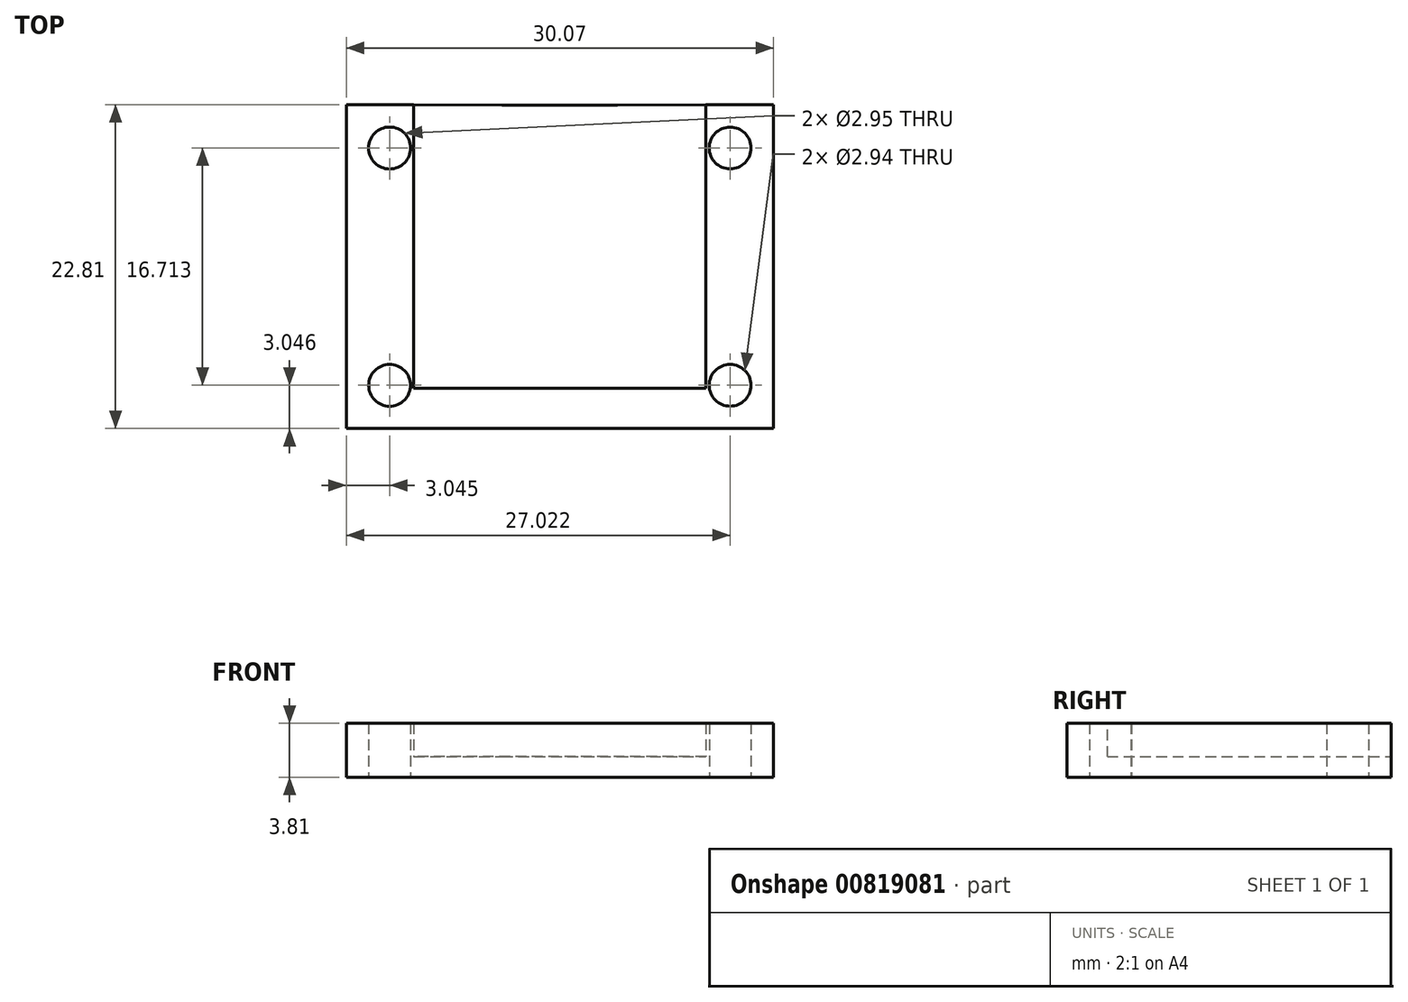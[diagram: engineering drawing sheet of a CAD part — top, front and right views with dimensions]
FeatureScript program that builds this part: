
annotation { "Feature Type Name" : "Feature", "Feature Type Description" : "" }
export const myFeature = defineFeature(function(context is Context, id is Id, definition is map)
    precondition{}
    {
        {
            var Q0;
            Q0=qCreatedBy(makeId("Top.planeOp"),FACE);
            var sketch = newSketch(context, id + "F0", { "sketchPlane" : qUnion([Q0])});
            skLineSegment(sketch, "E0.bottom", {"start": v(10.31, -9.2) * mm, "end": v(-10.31, -9.2) * mm});
            skLineSegment(sketch, "E0.left", {"start": v(10.31, -9.2) * mm, "end": v(10.31, 9.2) * mm});
            skLineSegment(sketch, "E0.right", {"start": v(-10.31, -9.2) * mm, "end": v(-10.31, 9.2) * mm});
            skPoint(sketch, "E0.middle", {"position": v(0, 0) * mm});
            skLineSegment(sketch, "E1.bottom", {"start": v(4.06, 3.08) * mm, "end": v(-4.06, 3.08) * mm});
            skLineSegment(sketch, "E1.left", {"start": v(4.06, 3.08) * mm, "end": v(4.06, 9.18) * mm});
            skLineSegment(sketch, "E1.right", {"start": v(-4.06, 3.08) * mm, "end": v(-4.06, 9.18) * mm});
            skPoint(sketch, "E1.middle", {"position": v(0, 6.13) * mm});
            skLineSegment(sketch, "E2", {"start": v(-10.31, 9.2) * mm, "end": v(-4.06, 9.18) * mm});
            skLineSegment(sketch, "E3", {"start": v(4.06, 9.18) * mm, "end": v(10.31, 9.2) * mm});
            skSolve(sketch);
        }
        {
            var Q0;
            Q0=makeQuery(id+"F0.imprint","IMPRINT",FACE,{"disambiguationData":[TD([[makeQuery(id+"F0.imprint","IMPRINT",EDGE,{"derivedFrom":sQuery(id+"F0.wireOp",EDGE,"E0.bottom")}),-1.0]])]});
            extrude(context, id + "F1", {"entities" : qUnion([Q0]), "depth" : 3.8 * mm, "offsetDistance" : 25.4 * mm});
        }
        {
            var Q0;
            Q0=makeQuery(id+"F1.opExtrude","SWEPT_FACE",FACE,{"disambiguationData":[OSD([sQuery(id+"F0.wireOp",EDGE,"E1.bottom")])]});
            var sketch = newSketch(context, id + "F2", { "sketchPlane" : qUnion([Q0])});
            skLineSegment(sketch, "E4.bottom", {"start": v(4.06, 3.81) * mm, "end": v(-4.06, 3.81) * mm});
            skLineSegment(sketch, "E4.top", {"start": v(4.06, 1.9) * mm, "end": v(-4.06, 1.9) * mm});
            skLineSegment(sketch, "E4.left", {"start": v(4.06, 3.81) * mm, "end": v(4.06, 1.9) * mm});
            skLineSegment(sketch, "E4.right", {"start": v(-4.06, 3.81) * mm, "end": v(-4.06, 1.9) * mm});
            skSolve(sketch);
        }
        {
            var Q0;
            Q0=makeQuery(id+"F2.imprint","IMPRINT",FACE,{"disambiguationData":[TD([[makeQuery(id+"F2.imprint","IMPRINT",EDGE,{"derivedFrom":sQuery(id+"F2.wireOp",EDGE,"E4.bottom")}),-1.0]])]});
            var Q1;
            Q1=makeQuery(id+"F1.opExtrude","SWEPT_FACE",FACE,{"disambiguationData":[OSD([sQuery(id+"F0.wireOp",EDGE,"E0.bottom")])]});
            extrude(context, id + "F3", {"entities" : qUnion([Q0, Q1]), "operationType" : NewBodyOperationType.ADD, "oppositeDirection" : true, "depth" : 1.85 * mm, "offsetDistance" : 25.4 * mm});
        }
        {
            var Q0;
            {var subQ0=sQuery(id+"F0.wireOp",EDGE,"E0.right");Q0=makeQuery(id+"F3.boolean.opBoolean","MERGE",FACE,{"derivedFrom":[makeQuery(id+"F1.opExtrude","SWEPT_FACE",FACE,{"disambiguationData":[OSD([subQ0])]}),makeQuery(id+"F3.opExtrude","SWEPT_FACE",FACE,{"disambiguationData":[OSD([sQuery(id+"F0.wireOp",EDGE,"E0.bottom"),subQ0])]})]});}
            extrude(context, id + "F4", {"entities" : qUnion([Q0]), "operationType" : NewBodyOperationType.ADD, "depth" : 2.18 * mm, "offsetDistance" : 25.4 * mm});
        }
        {
            var Q0;
            {var subQ0=sQuery(id+"F0.wireOp",EDGE,"E0.left");Q0=makeQuery(id+"F3.boolean.opBoolean","MERGE",FACE,{"derivedFrom":[makeQuery(id+"F1.opExtrude","SWEPT_FACE",FACE,{"disambiguationData":[OSD([subQ0])]}),makeQuery(id+"F3.opExtrude","SWEPT_FACE",FACE,{"disambiguationData":[OSD([sQuery(id+"F0.wireOp",EDGE,"E0.bottom"),subQ0])]})]});}
            extrude(context, id + "F5", {"entities" : qUnion([Q0]), "operationType" : NewBodyOperationType.ADD, "depth" : 2.18 * mm, "offsetDistance" : 25.4 * mm});
        }
        {
            var Q0;
            Q0=makeQuery(id+"F1.opExtrude","SWEPT_FACE",FACE,{"disambiguationData":[OSD([sQuery(id+"F0.wireOp",EDGE,"E1.bottom")])]});
            var sketch = newSketch(context, id + "F6", { "sketchPlane" : qUnion([Q0])});
            skLineSegment(sketch, "E5.bottom", {"start": v(-4.06, 3.81) * mm, "end": v(4.06, 3.81) * mm});
            skLineSegment(sketch, "E5.top", {"start": v(-4.06, 1.68) * mm, "end": v(4.06, 1.68) * mm});
            skLineSegment(sketch, "E5.left", {"start": v(-4.06, 3.81) * mm, "end": v(-4.06, 1.68) * mm});
            skLineSegment(sketch, "E5.right", {"start": v(4.06, 3.81) * mm, "end": v(4.06, 1.68) * mm});
            skSolve(sketch);
        }
        {
            var Q0;
            Q0=makeQuery(id+"F6.imprint","IMPRINT",FACE,{"disambiguationData":[TD([[makeQuery(id+"F6.imprint","IMPRINT",EDGE,{"derivedFrom":sQuery(id+"F6.wireOp",EDGE,"E5.bottom")}),-1.0]])]});
            extrude(context, id + "F7", {"entities" : qUnion([Q0]), "operationType" : NewBodyOperationType.ADD, "depth" : 6.1 * mm, "offsetDistance" : 25.4 * mm});
        }
        {
            var Q0;
            {var subQ0=sQuery(id+"F0.wireOp",EDGE,"E0.left");var subQ1=sQuery(id+"F0.wireOp",EDGE,"E0.bottom");var subQ2=sQuery(id+"F0.wireOp",EDGE,"E0.right");Q0=makeQuery(id+"F5.boolean.opBoolean","MERGE",FACE,{"derivedFrom":[makeQuery(id+"F4.boolean.opBoolean","MERGE",FACE,{"derivedFrom":[makeQuery(id+"F3.boolean.opBoolean","MERGE",FACE,{"derivedFrom":[makeQuery(id+"F1.opExtrude","CAP_FACE",FACE,{"disambiguationData":[OSD([subQ1,subQ0,subQ2,sQuery(id+"F0.wireOp",EDGE,"E1.bottom"),sQuery(id+"F0.wireOp",EDGE,"E1.left"),sQuery(id+"F0.wireOp",EDGE,"E1.right"),sQuery(id+"F0.wireOp",EDGE,"E2"),sQuery(id+"F0.wireOp",EDGE,"E3")])],"isStart":true}),makeQuery(id+"F3.opExtrude","SWEPT_FACE",FACE,{"disambiguationData":[OSD([subQ1]),TDD([makeQuery(id+"F1.opExtrude","CAP_EDGE",EDGE,{"disambiguationData":[OSD([subQ1])],"isStart":true})])]})]}),makeQuery(id+"F4.opExtrude","SWEPT_FACE",FACE,{"disambiguationData":[OSD([subQ1,subQ2]),TDD([makeQuery(id+"F3.boolean.opBoolean","MERGE",EDGE,{"derivedFrom":[makeQuery(id+"F1.opExtrude","CAP_EDGE",EDGE,{"disambiguationData":[OSD([subQ2])],"isStart":true}),makeQuery(id+"F3.opExtrude","SWEPT_EDGE",EDGE,{"disambiguationData":[OSD([subQ1,subQ2]),TDD([makeQuery(id+"F1.opExtrude","CAP_VERTEX",VERTEX,{"disambiguationData":[OSD([subQ1,subQ2])],"isStart":true})])]})]})])]})]}),makeQuery(id+"F5.opExtrude","SWEPT_FACE",FACE,{"disambiguationData":[OSD([subQ1,subQ0]),TDD([makeQuery(id+"F3.boolean.opBoolean","MERGE",EDGE,{"derivedFrom":[makeQuery(id+"F1.opExtrude","CAP_EDGE",EDGE,{"disambiguationData":[OSD([subQ0])],"isStart":true}),makeQuery(id+"F3.opExtrude","SWEPT_EDGE",EDGE,{"disambiguationData":[OSD([subQ1,subQ0]),TDD([makeQuery(id+"F1.opExtrude","CAP_VERTEX",VERTEX,{"disambiguationData":[OSD([subQ1,subQ0])],"isStart":true})])]})]})])]})]});}
            var sketch = newSketch(context, id + "F8", { "sketchPlane" : qUnion([Q0])});
            skLineSegment(sketch, "E6.bottom", {"start": v(-9.07, 8.52) * mm, "end": v(9.07, 8.52) * mm});
            skLineSegment(sketch, "E6.top", {"start": v(-9.07, 0) * mm, "end": v(9.07, 0) * mm});
            skLineSegment(sketch, "E6.left", {"start": v(-9.07, 8.52) * mm, "end": v(-9.07, 0) * mm});
            skLineSegment(sketch, "E6.right", {"start": v(9.07, 8.52) * mm, "end": v(9.07, 0) * mm});
            skSolve(sketch);
        }
        {
            var Q0;
            Q0=makeQuery(id+"F8.imprint","IMPRINT",FACE,{"disambiguationData":[TD([[makeQuery(id+"F8.imprint","IMPRINT",EDGE,{"derivedFrom":sQuery(id+"F8.wireOp",EDGE,"E6.bottom")}),-1.0]])]});
            extrude(context, id + "F9", {"entities" : qUnion([Q0]), "operationType" : NewBodyOperationType.REMOVE, "oppositeDirection" : true, "depth" : 1.55 * mm, "offsetDistance" : 25.4 * mm});
        }
        {
            var Q0;
            {var subQ0=sQuery(id+"F0.wireOp",EDGE,"E0.left");var subQ1=sQuery(id+"F0.wireOp",EDGE,"E0.bottom");var subQ2=sQuery(id+"F0.wireOp",EDGE,"E0.right");Q0=makeQuery(id+"F7.boolean.opBoolean","MERGE",FACE,{"derivedFrom":[makeQuery(id+"F5.boolean.opBoolean","MERGE",FACE,{"derivedFrom":[makeQuery(id+"F4.boolean.opBoolean","MERGE",FACE,{"derivedFrom":[makeQuery(id+"F3.boolean.opBoolean","MERGE",FACE,{"derivedFrom":[makeQuery(id+"F1.opExtrude","CAP_FACE",FACE,{"disambiguationData":[OSD([subQ1,subQ0,subQ2,sQuery(id+"F0.wireOp",EDGE,"E1.bottom"),sQuery(id+"F0.wireOp",EDGE,"E1.left"),sQuery(id+"F0.wireOp",EDGE,"E1.right"),sQuery(id+"F0.wireOp",EDGE,"E2"),sQuery(id+"F0.wireOp",EDGE,"E3")])],"isStart":false}),makeQuery(id+"F3.opExtrude","SWEPT_FACE",FACE,{"disambiguationData":[OSD([subQ1]),TDD([makeQuery(id+"F1.opExtrude","CAP_EDGE",EDGE,{"disambiguationData":[OSD([subQ1])],"isStart":false})])]})]}),makeQuery(id+"F4.opExtrude","SWEPT_FACE",FACE,{"disambiguationData":[OSD([subQ1,subQ2]),TDD([makeQuery(id+"F3.boolean.opBoolean","MERGE",EDGE,{"derivedFrom":[makeQuery(id+"F1.opExtrude","CAP_EDGE",EDGE,{"disambiguationData":[OSD([subQ2])],"isStart":false}),makeQuery(id+"F3.opExtrude","SWEPT_EDGE",EDGE,{"disambiguationData":[OSD([subQ1,subQ2]),TDD([makeQuery(id+"F1.opExtrude","CAP_VERTEX",VERTEX,{"disambiguationData":[OSD([subQ1,subQ2])],"isStart":false})])]})]})])]})]}),makeQuery(id+"F5.opExtrude","SWEPT_FACE",FACE,{"disambiguationData":[OSD([subQ1,subQ0]),TDD([makeQuery(id+"F3.boolean.opBoolean","MERGE",EDGE,{"derivedFrom":[makeQuery(id+"F1.opExtrude","CAP_EDGE",EDGE,{"disambiguationData":[OSD([subQ0])],"isStart":false}),makeQuery(id+"F3.opExtrude","SWEPT_EDGE",EDGE,{"disambiguationData":[OSD([subQ1,subQ0]),TDD([makeQuery(id+"F1.opExtrude","CAP_VERTEX",VERTEX,{"disambiguationData":[OSD([subQ1,subQ0])],"isStart":false})])]})]})])]})]}),makeQuery(id+"F7.opExtrude","SWEPT_FACE",FACE,{"disambiguationData":[OSD([sQuery(id+"F6.wireOp",EDGE,"E5.bottom")])]})]});}
            var sketch = newSketch(context, id + "F10", { "sketchPlane" : qUnion([Q0])});
            skLineSegment(sketch, "E7.bottom", {"start": v(-12.5, 9.2) * mm, "end": v(12.5, 9.2) * mm});
            skLineSegment(sketch, "E7.top", {"start": v(-12.5, -11.06) * mm, "end": v(12.5, -11.06) * mm});
            skLineSegment(sketch, "E7.left", {"start": v(-12.5, 9.2) * mm, "end": v(-12.5, -11.06) * mm});
            skLineSegment(sketch, "E7.right", {"start": v(12.5, 9.2) * mm, "end": v(12.5, -11.06) * mm});
            skSolve(sketch);
        }
        {
            var Q0;
            Q0=makeQuery(id+"F4.opExtrude","CAP_FACE",FACE,{"disambiguationData":[OSD([sQuery(id+"F0.wireOp",EDGE,"E0.bottom"),sQuery(id+"F0.wireOp",EDGE,"E0.right")])],"isStart":false});
            extrude(context, id + "F11", {"entities" : qUnion([Q0]), "operationType" : NewBodyOperationType.ADD, "depth" : 2.54 * mm, "offsetDistance" : 25.4 * mm});
        }
        {
            var Q0;
            Q0=makeQuery(id+"F5.opExtrude","CAP_FACE",FACE,{"disambiguationData":[OSD([sQuery(id+"F0.wireOp",EDGE,"E0.bottom"),sQuery(id+"F0.wireOp",EDGE,"E0.left")])],"isStart":false});
            extrude(context, id + "F12", {"entities" : qUnion([Q0]), "operationType" : NewBodyOperationType.ADD, "depth" : 2.54 * mm, "offsetDistance" : 25.4 * mm});
        }
        {
            var Q0;
            {var subQ0=sQuery(id+"F0.wireOp",EDGE,"E0.left");var subQ1=sQuery(id+"F0.wireOp",EDGE,"E0.bottom");var subQ2=makeQuery(id+"F3.opExtrude","CAP_EDGE",EDGE,{"disambiguationData":[OSD([subQ1,subQ0])],"isStart":false});var subQ3=sQuery(id+"F0.wireOp",EDGE,"E0.right");var subQ4=makeQuery(id+"F3.opExtrude","CAP_EDGE",EDGE,{"disambiguationData":[OSD([subQ1,subQ3])],"isStart":false});Q0=makeQuery(id+"F12.boolean.opBoolean","MERGE",FACE,{"derivedFrom":[makeQuery(id+"F11.boolean.opBoolean","MERGE",FACE,{"derivedFrom":[makeQuery(id+"F5.boolean.opBoolean","MERGE",FACE,{"derivedFrom":[makeQuery(id+"F4.boolean.opBoolean","MERGE",FACE,{"derivedFrom":[makeQuery(id+"F3.opExtrude","CAP_FACE",FACE,{"disambiguationData":[OSD([subQ1])],"isStart":false}),makeQuery(id+"F4.opExtrude","SWEPT_FACE",FACE,{"disambiguationData":[OSD([subQ1,subQ3]),TDD([subQ4])]})]}),makeQuery(id+"F5.opExtrude","SWEPT_FACE",FACE,{"disambiguationData":[OSD([subQ1,subQ0]),TDD([subQ2])]})]}),makeQuery(id+"F11.opExtrude","SWEPT_FACE",FACE,{"disambiguationData":[OSD([subQ1,subQ3]),TDD([makeQuery(id+"F4.opExtrude","CAP_EDGE",EDGE,{"disambiguationData":[OSD([subQ1,subQ3]),TDD([subQ4])],"isStart":false})])]})]}),makeQuery(id+"F12.opExtrude","SWEPT_FACE",FACE,{"disambiguationData":[OSD([subQ1,subQ0]),TDD([makeQuery(id+"F5.opExtrude","CAP_EDGE",EDGE,{"disambiguationData":[OSD([subQ1,subQ0]),TDD([subQ2])],"isStart":false})])]})]});}
            extrude(context, id + "F13", {"entities" : qUnion([Q0]), "operationType" : NewBodyOperationType.ADD, "depth" : 2.54 * mm, "offsetDistance" : 25.4 * mm});
        }
        {
            var Q0;
            Q0=makeQuery(id+"F9.boolean.opBoolean","COPY",FACE,{"derivedFrom":makeQuery(id+"F9.opExtrude","CAP_FACE",FACE,{"disambiguationData":[OSD([sQuery(id+"F8.wireOp",EDGE,"E6.bottom"),sQuery(id+"F8.wireOp",EDGE,"E6.top"),sQuery(id+"F8.wireOp",EDGE,"E6.left"),sQuery(id+"F8.wireOp",EDGE,"E6.right")])],"isStart":false})});
            extrude(context, id + "F14", {"entities" : qUnion([Q0]), "operationType" : NewBodyOperationType.REMOVE, "oppositeDirection" : true, "depth" : 0.81 * mm, "offsetDistance" : 25.4 * mm});
        }
        {
            var Q0;
            Q0=makeQuery(id+"F1.opExtrude","SWEPT_BODY",BODY,{"disambiguationData":[OSD([sQuery(id+"F0.wireOp",EDGE,"E0.bottom"),sQuery(id+"F0.wireOp",EDGE,"E0.left"),sQuery(id+"F0.wireOp",EDGE,"E0.right"),sQuery(id+"F0.wireOp",EDGE,"E1.bottom"),sQuery(id+"F0.wireOp",EDGE,"E1.left"),sQuery(id+"F0.wireOp",EDGE,"E1.right"),sQuery(id+"F0.wireOp",EDGE,"E2"),sQuery(id+"F0.wireOp",EDGE,"E3")])]});
            var Q1;
            Q1=sQuery(id+"F10.wireOp",EDGE,"E7.right");
            transform(context, id + "F15", {"entities" : qUnion([Q0]), "transformType" : TransformType.ROTATION, "transformAxis" : qUnion([Q1]), "angle" : 180 * degree, "oppositeDirection" : true, "makeCopy" : false});
        }
        {
            var Q0;
            {var subQ0=sQuery(id+"F8.wireOp",EDGE,"E6.bottom");Q0=makeQuery(id+"F14.boolean.opBoolean","MERGE",FACE,{"derivedFrom":[makeQuery(id+"F9.boolean.opBoolean","COPY",FACE,{"derivedFrom":makeQuery(id+"F9.opExtrude","SWEPT_FACE",FACE,{"disambiguationData":[OSD([subQ0])]})}),makeQuery(id+"F14.opExtrude","SWEPT_FACE",FACE,{"disambiguationData":[OSD([subQ0])]})]});}
            extrude(context, id + "F16", {"entities" : qUnion([Q0]), "operationType" : NewBodyOperationType.REMOVE, "oppositeDirection" : true, "depth" : 2.24 * mm, "offsetDistance" : 25.4 * mm});
        }
        {
            var Q0;
            {var subQ0=sQuery(id+"F0.wireOp",EDGE,"E0.left");var subQ1=sQuery(id+"F0.wireOp",EDGE,"E0.bottom");var subQ2=makeQuery(id+"F1.opExtrude","CAP_VERTEX",VERTEX,{"disambiguationData":[OSD([subQ1,subQ0])],"isStart":false});var subQ3=makeQuery(id+"F3.opExtrude","CAP_VERTEX",VERTEX,{"disambiguationData":[OSD([subQ1,subQ0]),TDD([subQ2])],"isStart":false});var subQ4=sQuery(id+"F0.wireOp",EDGE,"E0.right");var subQ5=makeQuery(id+"F1.opExtrude","CAP_VERTEX",VERTEX,{"disambiguationData":[OSD([subQ1,subQ4])],"isStart":false});var subQ6=makeQuery(id+"F3.opExtrude","CAP_VERTEX",VERTEX,{"disambiguationData":[OSD([subQ1,subQ4]),TDD([subQ5])],"isStart":false});var subQ7=makeQuery(id+"F1.opExtrude","CAP_EDGE",EDGE,{"disambiguationData":[OSD([subQ1])],"isStart":false});var subQ8=makeQuery(id+"F3.boolean.opBoolean","MERGE",EDGE,{"derivedFrom":[makeQuery(id+"F1.opExtrude","CAP_EDGE",EDGE,{"disambiguationData":[OSD([subQ0])],"isStart":false}),makeQuery(id+"F3.opExtrude","SWEPT_EDGE",EDGE,{"disambiguationData":[OSD([subQ1,subQ0]),TDD([subQ2])]})]});var subQ9=makeQuery(id+"F3.boolean.opBoolean","MERGE",EDGE,{"derivedFrom":[makeQuery(id+"F1.opExtrude","CAP_EDGE",EDGE,{"disambiguationData":[OSD([subQ4])],"isStart":false}),makeQuery(id+"F3.opExtrude","SWEPT_EDGE",EDGE,{"disambiguationData":[OSD([subQ1,subQ4]),TDD([subQ5])]})]});Q0=makeQuery(id+"F13.boolean.opBoolean","MERGE",FACE,{"derivedFrom":[makeQuery(id+"F12.boolean.opBoolean","MERGE",FACE,{"derivedFrom":[makeQuery(id+"F11.boolean.opBoolean","MERGE",FACE,{"derivedFrom":[makeQuery(id+"F7.boolean.opBoolean","MERGE",FACE,{"derivedFrom":[makeQuery(id+"F5.boolean.opBoolean","MERGE",FACE,{"derivedFrom":[makeQuery(id+"F4.boolean.opBoolean","MERGE",FACE,{"derivedFrom":[makeQuery(id+"F3.boolean.opBoolean","MERGE",FACE,{"derivedFrom":[makeQuery(id+"F1.opExtrude","CAP_FACE",FACE,{"disambiguationData":[OSD([subQ1,subQ0,subQ4,sQuery(id+"F0.wireOp",EDGE,"E1.bottom"),sQuery(id+"F0.wireOp",EDGE,"E1.left"),sQuery(id+"F0.wireOp",EDGE,"E1.right"),sQuery(id+"F0.wireOp",EDGE,"E2"),sQuery(id+"F0.wireOp",EDGE,"E3")])],"isStart":false}),makeQuery(id+"F3.opExtrude","SWEPT_FACE",FACE,{"disambiguationData":[OSD([subQ1]),TDD([subQ7])]})]}),makeQuery(id+"F4.opExtrude","SWEPT_FACE",FACE,{"disambiguationData":[OSD([subQ1,subQ4]),TDD([subQ9])]})]}),makeQuery(id+"F5.opExtrude","SWEPT_FACE",FACE,{"disambiguationData":[OSD([subQ1,subQ0]),TDD([subQ8])]})]}),makeQuery(id+"F7.opExtrude","SWEPT_FACE",FACE,{"disambiguationData":[OSD([sQuery(id+"F6.wireOp",EDGE,"E5.bottom")])]})]}),makeQuery(id+"F11.opExtrude","SWEPT_FACE",FACE,{"disambiguationData":[OSD([subQ1,subQ4]),TDD([makeQuery(id+"F4.opExtrude","CAP_EDGE",EDGE,{"disambiguationData":[OSD([subQ1,subQ4]),TDD([subQ9])],"isStart":false})])]})]}),makeQuery(id+"F12.opExtrude","SWEPT_FACE",FACE,{"disambiguationData":[OSD([subQ1,subQ0]),TDD([makeQuery(id+"F5.opExtrude","CAP_EDGE",EDGE,{"disambiguationData":[OSD([subQ1,subQ0]),TDD([subQ8])],"isStart":false})])]})]}),makeQuery(id+"F13.opExtrude","SWEPT_FACE",FACE,{"disambiguationData":[OSD([subQ1,subQ0,subQ4]),TDD([makeQuery(id+"F12.boolean.opBoolean","MERGE",EDGE,{"derivedFrom":[makeQuery(id+"F11.boolean.opBoolean","MERGE",EDGE,{"derivedFrom":[makeQuery(id+"F5.boolean.opBoolean","MERGE",EDGE,{"derivedFrom":[makeQuery(id+"F4.boolean.opBoolean","MERGE",EDGE,{"derivedFrom":[makeQuery(id+"F3.opExtrude","CAP_EDGE",EDGE,{"disambiguationData":[OSD([subQ1]),TDD([subQ7])],"isStart":false}),makeQuery(id+"F4.opExtrude","SWEPT_EDGE",EDGE,{"disambiguationData":[OSD([subQ1,subQ4]),TDD([subQ6])]})]}),makeQuery(id+"F5.opExtrude","SWEPT_EDGE",EDGE,{"disambiguationData":[OSD([subQ1,subQ0]),TDD([subQ3])]})]}),makeQuery(id+"F11.opExtrude","SWEPT_EDGE",EDGE,{"disambiguationData":[OSD([subQ1,subQ4]),TDD([makeQuery(id+"F4.opExtrude","CAP_VERTEX",VERTEX,{"disambiguationData":[OSD([subQ1,subQ4]),TDD([subQ6])],"isStart":false})])]})]}),makeQuery(id+"F12.opExtrude","SWEPT_EDGE",EDGE,{"disambiguationData":[OSD([subQ1,subQ0]),TDD([makeQuery(id+"F5.opExtrude","CAP_VERTEX",VERTEX,{"disambiguationData":[OSD([subQ1,subQ0]),TDD([subQ3])],"isStart":false})])]})]})])]})]});}
            var sketch = newSketch(context, id + "F17", { "sketchPlane" : qUnion([Q0])});
            skCircle(sketch, "E8", {"center": v(13, 10.55) * mm, "radius": 1.47 * mm});
            skCircle(sketch, "E9", {"center": v(36.98, 10.55) * mm, "radius": 1.47 * mm});
            skCircle(sketch, "E10", {"center": v(13, -6.16) * mm, "radius": 1.48 * mm});
            skCircle(sketch, "E11", {"center": v(36.98, -6.16) * mm, "radius": 1.47 * mm});
            skSolve(sketch);
        }
        {
            var Q0;
            Q0=makeQuery(id+"F17.imprint","IMPRINT",FACE,{"disambiguationData":[TD([[makeQuery(id+"F17.imprint","IMPRINT",EDGE,{"derivedFrom":sQuery(id+"F17.wireOp",EDGE,"E8")}),1.0]])]});
            var Q1;
            Q1=makeQuery(id+"F17.imprint","IMPRINT",FACE,{"disambiguationData":[TD([[makeQuery(id+"F17.imprint","IMPRINT",EDGE,{"derivedFrom":sQuery(id+"F17.wireOp",EDGE,"E9")}),1.0]])]});
            var Q2;
            Q2=makeQuery(id+"F17.imprint","IMPRINT",FACE,{"disambiguationData":[TD([[makeQuery(id+"F17.imprint","IMPRINT",EDGE,{"derivedFrom":sQuery(id+"F17.wireOp",EDGE,"E10")}),1.0]])]});
            var Q3;
            Q3=makeQuery(id+"F17.imprint","IMPRINT",FACE,{"disambiguationData":[TD([[makeQuery(id+"F17.imprint","IMPRINT",EDGE,{"derivedFrom":sQuery(id+"F17.wireOp",EDGE,"E11")}),1.0]])]});
            extrude(context, id + "F18", {"entities" : qUnion([Q0, Q1, Q2, Q3]), "operationType" : NewBodyOperationType.REMOVE, "oppositeDirection" : true, "depth" : 25.4 * mm, "offsetDistance" : 25.4 * mm});
        }
        {
            var Q0;
            Q0=makeQuery(id+"F1.opExtrude","SWEPT_BODY",BODY,{"disambiguationData":[OSD([sQuery(id+"F0.wireOp",EDGE,"E0.bottom"),sQuery(id+"F0.wireOp",EDGE,"E0.left"),sQuery(id+"F0.wireOp",EDGE,"E0.right"),sQuery(id+"F0.wireOp",EDGE,"E1.bottom"),sQuery(id+"F0.wireOp",EDGE,"E1.left"),sQuery(id+"F0.wireOp",EDGE,"E1.right"),sQuery(id+"F0.wireOp",EDGE,"E2"),sQuery(id+"F0.wireOp",EDGE,"E3")])]});
            transform(context, id + "F19", {"entities" : qUnion([Q0]), "transformType" : TransformType.TRANSLATION_3D, "dx" : 0 * mm, "dy" : -28.96 * mm, "dz" : 0 * mm, "makeCopy" : true});
        }
        {
            var Q0;
            Q0=makeQuery(id+"F19.opPattern","COPY",BODY,{"derivedFrom":makeQuery(id+"F1.opExtrude","SWEPT_BODY",BODY,{"disambiguationData":[OSD([sQuery(id+"F0.wireOp",EDGE,"E0.bottom"),sQuery(id+"F0.wireOp",EDGE,"E0.left"),sQuery(id+"F0.wireOp",EDGE,"E0.right"),sQuery(id+"F0.wireOp",EDGE,"E1.bottom"),sQuery(id+"F0.wireOp",EDGE,"E1.left"),sQuery(id+"F0.wireOp",EDGE,"E1.right"),sQuery(id+"F0.wireOp",EDGE,"E2"),sQuery(id+"F0.wireOp",EDGE,"E3")])]}),"instanceName":"1"});
            deleteBodies(context, id + "F20", {"entities" : qUnion([Q0])});
        }
        {
            var Q0;
            {var subQ0=sQuery(id+"F0.wireOp",EDGE,"E0.left");var subQ1=sQuery(id+"F0.wireOp",EDGE,"E0.bottom");var subQ2=makeQuery(id+"F1.opExtrude","CAP_VERTEX",VERTEX,{"disambiguationData":[OSD([subQ1,subQ0])],"isStart":true});var subQ3=makeQuery(id+"F3.opExtrude","CAP_VERTEX",VERTEX,{"disambiguationData":[OSD([subQ1,subQ0]),TDD([subQ2])],"isStart":false});var subQ4=sQuery(id+"F0.wireOp",EDGE,"E0.right");var subQ5=makeQuery(id+"F1.opExtrude","CAP_VERTEX",VERTEX,{"disambiguationData":[OSD([subQ1,subQ4])],"isStart":true});var subQ6=makeQuery(id+"F3.opExtrude","CAP_VERTEX",VERTEX,{"disambiguationData":[OSD([subQ1,subQ4]),TDD([subQ5])],"isStart":false});var subQ7=makeQuery(id+"F1.opExtrude","CAP_EDGE",EDGE,{"disambiguationData":[OSD([subQ1])],"isStart":true});var subQ8=makeQuery(id+"F3.boolean.opBoolean","MERGE",EDGE,{"derivedFrom":[makeQuery(id+"F1.opExtrude","CAP_EDGE",EDGE,{"disambiguationData":[OSD([subQ0])],"isStart":true}),makeQuery(id+"F3.opExtrude","SWEPT_EDGE",EDGE,{"disambiguationData":[OSD([subQ1,subQ0]),TDD([subQ2])]})]});var subQ9=makeQuery(id+"F3.boolean.opBoolean","MERGE",EDGE,{"derivedFrom":[makeQuery(id+"F1.opExtrude","CAP_EDGE",EDGE,{"disambiguationData":[OSD([subQ4])],"isStart":true}),makeQuery(id+"F3.opExtrude","SWEPT_EDGE",EDGE,{"disambiguationData":[OSD([subQ1,subQ4]),TDD([subQ5])]})]});Q0=makeQuery(id+"F13.boolean.opBoolean","MERGE",FACE,{"derivedFrom":[makeQuery(id+"F12.boolean.opBoolean","MERGE",FACE,{"derivedFrom":[makeQuery(id+"F11.boolean.opBoolean","MERGE",FACE,{"derivedFrom":[makeQuery(id+"F5.boolean.opBoolean","MERGE",FACE,{"derivedFrom":[makeQuery(id+"F4.boolean.opBoolean","MERGE",FACE,{"derivedFrom":[makeQuery(id+"F3.boolean.opBoolean","MERGE",FACE,{"derivedFrom":[makeQuery(id+"F1.opExtrude","CAP_FACE",FACE,{"disambiguationData":[OSD([subQ1,subQ0,subQ4,sQuery(id+"F0.wireOp",EDGE,"E1.bottom"),sQuery(id+"F0.wireOp",EDGE,"E1.left"),sQuery(id+"F0.wireOp",EDGE,"E1.right"),sQuery(id+"F0.wireOp",EDGE,"E2"),sQuery(id+"F0.wireOp",EDGE,"E3")])],"isStart":true}),makeQuery(id+"F3.opExtrude","SWEPT_FACE",FACE,{"disambiguationData":[OSD([subQ1]),TDD([subQ7])]})]}),makeQuery(id+"F4.opExtrude","SWEPT_FACE",FACE,{"disambiguationData":[OSD([subQ1,subQ4]),TDD([subQ9])]})]}),makeQuery(id+"F5.opExtrude","SWEPT_FACE",FACE,{"disambiguationData":[OSD([subQ1,subQ0]),TDD([subQ8])]})]}),makeQuery(id+"F11.opExtrude","SWEPT_FACE",FACE,{"disambiguationData":[OSD([subQ1,subQ4]),TDD([makeQuery(id+"F4.opExtrude","CAP_EDGE",EDGE,{"disambiguationData":[OSD([subQ1,subQ4]),TDD([subQ9])],"isStart":false})])]})]}),makeQuery(id+"F12.opExtrude","SWEPT_FACE",FACE,{"disambiguationData":[OSD([subQ1,subQ0]),TDD([makeQuery(id+"F5.opExtrude","CAP_EDGE",EDGE,{"disambiguationData":[OSD([subQ1,subQ0]),TDD([subQ8])],"isStart":false})])]})]}),makeQuery(id+"F13.opExtrude","SWEPT_FACE",FACE,{"disambiguationData":[OSD([subQ1,subQ0,subQ4]),TDD([makeQuery(id+"F12.boolean.opBoolean","MERGE",EDGE,{"derivedFrom":[makeQuery(id+"F11.boolean.opBoolean","MERGE",EDGE,{"derivedFrom":[makeQuery(id+"F5.boolean.opBoolean","MERGE",EDGE,{"derivedFrom":[makeQuery(id+"F4.boolean.opBoolean","MERGE",EDGE,{"derivedFrom":[makeQuery(id+"F3.opExtrude","CAP_EDGE",EDGE,{"disambiguationData":[OSD([subQ1]),TDD([subQ7])],"isStart":false}),makeQuery(id+"F4.opExtrude","SWEPT_EDGE",EDGE,{"disambiguationData":[OSD([subQ1,subQ4]),TDD([subQ6])]})]}),makeQuery(id+"F5.opExtrude","SWEPT_EDGE",EDGE,{"disambiguationData":[OSD([subQ1,subQ0]),TDD([subQ3])]})]}),makeQuery(id+"F11.opExtrude","SWEPT_EDGE",EDGE,{"disambiguationData":[OSD([subQ1,subQ4]),TDD([makeQuery(id+"F4.opExtrude","CAP_VERTEX",VERTEX,{"disambiguationData":[OSD([subQ1,subQ4]),TDD([subQ6])],"isStart":false})])]})]}),makeQuery(id+"F12.opExtrude","SWEPT_EDGE",EDGE,{"disambiguationData":[OSD([subQ1,subQ0]),TDD([makeQuery(id+"F5.opExtrude","CAP_VERTEX",VERTEX,{"disambiguationData":[OSD([subQ1,subQ0]),TDD([subQ3])],"isStart":false})])]})]})])]})]});}
            var sketch = newSketch(context, id + "F21", { "sketchPlane" : qUnion([Q0])});
            skLineSegment(sketch, "E12.bottom", {"start": v(29.06, 9.18) * mm, "end": v(20.93, 9.18) * mm});
            skLineSegment(sketch, "E12.top", {"start": v(29.06, 3.08) * mm, "end": v(20.93, 3.08) * mm});
            skLineSegment(sketch, "E12.left", {"start": v(29.06, 9.18) * mm, "end": v(29.06, 3.08) * mm});
            skLineSegment(sketch, "E12.right", {"start": v(20.93, 9.18) * mm, "end": v(20.93, 3.08) * mm});
            skSolve(sketch);
        }
        {
            var Q0;
            Q0=makeQuery(id+"F21.imprint","IMPRINT",FACE,{"disambiguationData":[TD([[makeQuery(id+"F21.imprint","IMPRINT",EDGE,{"derivedFrom":sQuery(id+"F21.wireOp",EDGE,"E12.bottom")}),1.0]])]});
            extrude(context, id + "F22", {"entities" : qUnion([Q0]), "operationType" : NewBodyOperationType.ADD, "oppositeDirection" : true, "depth" : 1.65 * mm, "offsetDistance" : 25.4 * mm});
        }
        {
            var Q0;
            {var subQ0=sQuery(id+"F8.wireOp",EDGE,"E6.top");Q0=makeQuery(id+"F14.boolean.opBoolean","MERGE",FACE,{"derivedFrom":[makeQuery(id+"F9.boolean.opBoolean","COPY",FACE,{"derivedFrom":makeQuery(id+"F9.opExtrude","SWEPT_FACE",FACE,{"disambiguationData":[OSD([subQ0])]})}),makeQuery(id+"F14.opExtrude","SWEPT_FACE",FACE,{"disambiguationData":[OSD([subQ0])]})]});}
            extrude(context, id + "F23", {"entities" : qUnion([Q0]), "operationType" : NewBodyOperationType.REMOVE, "oppositeDirection" : true, "depth" : 13.92 * mm, "offsetDistance" : 25.4 * mm});
        }
        {
            var Q0;
            {var subQ0=sQuery(id+"F8.wireOp",EDGE,"E6.left");Q0=makeQuery(id+"F23.boolean.opBoolean","MERGE",FACE,{"derivedFrom":[makeQuery(id+"F16.boolean.opBoolean","MERGE",FACE,{"derivedFrom":[makeQuery(id+"F14.boolean.opBoolean","MERGE",FACE,{"derivedFrom":[makeQuery(id+"F9.boolean.opBoolean","COPY",FACE,{"derivedFrom":makeQuery(id+"F9.opExtrude","SWEPT_FACE",FACE,{"disambiguationData":[OSD([subQ0])]})}),makeQuery(id+"F14.opExtrude","SWEPT_FACE",FACE,{"disambiguationData":[OSD([subQ0])]})]}),makeQuery(id+"F16.opExtrude","SWEPT_FACE",FACE,{"disambiguationData":[OSD([sQuery(id+"F8.wireOp",EDGE,"E6.bottom"),subQ0])]})]}),makeQuery(id+"F23.opExtrude","SWEPT_FACE",FACE,{"disambiguationData":[OSD([sQuery(id+"F8.wireOp",EDGE,"E6.top"),subQ0])]})]});}
            extrude(context, id + "F24", {"entities" : qUnion([Q0]), "operationType" : NewBodyOperationType.REMOVE, "oppositeDirection" : true, "depth" : 1.22 * mm, "offsetDistance" : 25.4 * mm});
        }
        {
            var Q0;
            {var subQ0=sQuery(id+"F8.wireOp",EDGE,"E6.right");Q0=makeQuery(id+"F23.boolean.opBoolean","MERGE",FACE,{"derivedFrom":[makeQuery(id+"F16.boolean.opBoolean","MERGE",FACE,{"derivedFrom":[makeQuery(id+"F14.boolean.opBoolean","MERGE",FACE,{"derivedFrom":[makeQuery(id+"F9.boolean.opBoolean","COPY",FACE,{"derivedFrom":makeQuery(id+"F9.opExtrude","SWEPT_FACE",FACE,{"disambiguationData":[OSD([subQ0])]})}),makeQuery(id+"F14.opExtrude","SWEPT_FACE",FACE,{"disambiguationData":[OSD([subQ0])]})]}),makeQuery(id+"F16.opExtrude","SWEPT_FACE",FACE,{"disambiguationData":[OSD([sQuery(id+"F8.wireOp",EDGE,"E6.bottom"),subQ0])]})]}),makeQuery(id+"F23.opExtrude","SWEPT_FACE",FACE,{"disambiguationData":[OSD([sQuery(id+"F8.wireOp",EDGE,"E6.top"),subQ0])]})]});}
            extrude(context, id + "F25", {"entities" : qUnion([Q0]), "operationType" : NewBodyOperationType.REMOVE, "oppositeDirection" : true, "depth" : 1.22 * mm, "offsetDistance" : 25.4 * mm});
        }
    });
